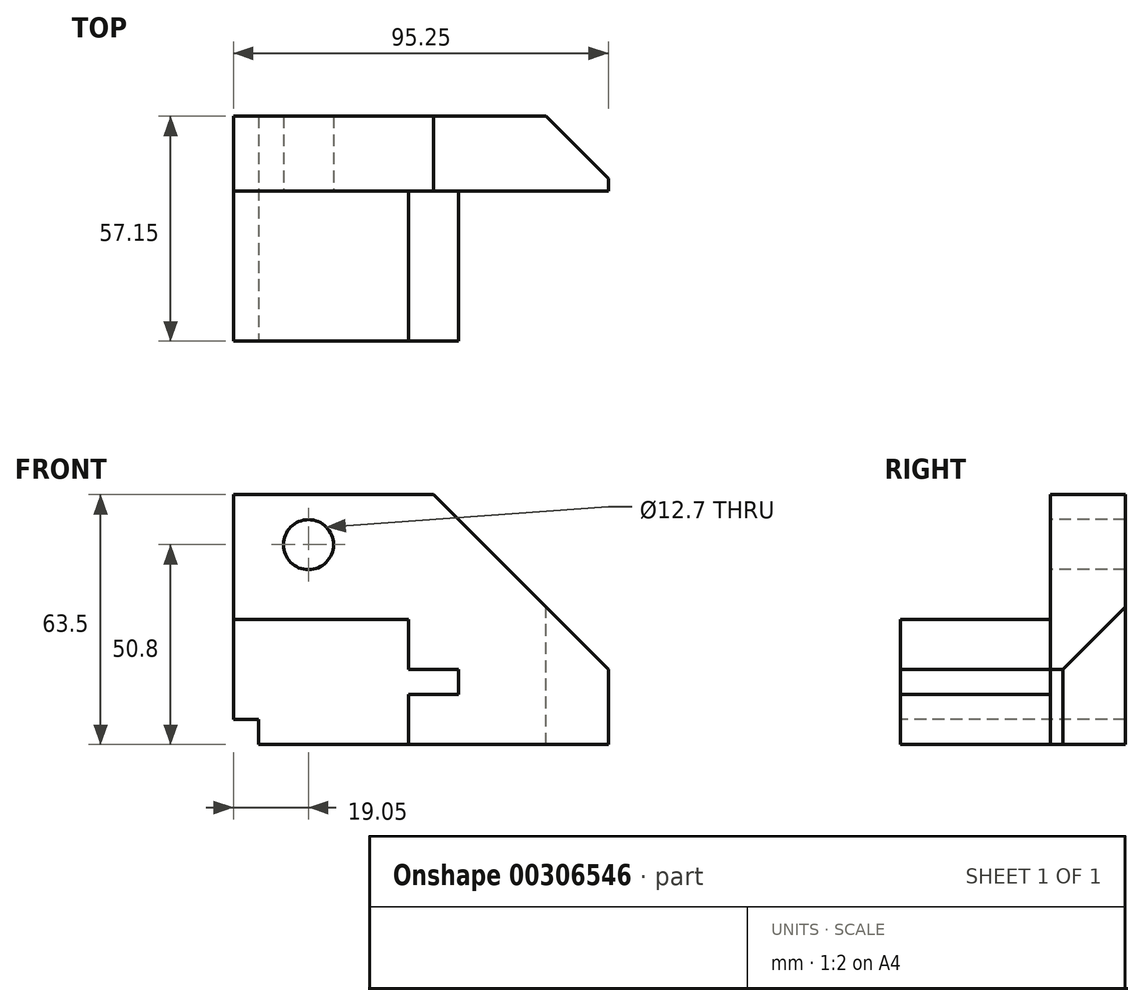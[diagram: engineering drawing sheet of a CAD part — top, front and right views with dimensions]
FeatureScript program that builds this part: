
annotation { "Feature Type Name" : "Feature", "Feature Type Description" : "" }
export const myFeature = defineFeature(function(context is Context, id is Id, definition is map)
    precondition{}
    {
        {
            var Q0;
            Q0=qCreatedBy(makeId("Front.planeOp"),FACE);
            var sketch = newSketch(context, id + "F0", { "sketchPlane" : qUnion([Q0])});
            skLineSegment(sketch, "E0.bottom", {"start": v(0, 0) * mm, "end": v(107.95, 0) * mm});
            skLineSegment(sketch, "E0.top", {"start": v(0, 63.5) * mm, "end": v(107.95, 63.5) * mm});
            skLineSegment(sketch, "E0.left", {"start": v(0, 0) * mm, "end": v(0, 63.5) * mm});
            skLineSegment(sketch, "E0.right", {"start": v(107.95, 0) * mm, "end": v(107.95, 63.5) * mm});
            skSolve(sketch);
        }
        {
            var Q0;
            Q0=makeQuery(id+"F0.imprint","IMPRINT",FACE,{"disambiguationData":[TD([[makeQuery(id+"F0.imprint","IMPRINT",EDGE,{"derivedFrom":sQuery(id+"F0.wireOp",EDGE,"E0.bottom")}),1.0]])]});
            extrude(context, id + "F1", {"entities" : qUnion([Q0]), "depth" : 57.15 * mm});
        }
        {
            var Q0;
            Q0=makeQuery(id+"F1.opExtrude","CAP_FACE",FACE,{"disambiguationData":[OSD([sQuery(id+"F0.wireOp",EDGE,"E0.bottom"),sQuery(id+"F0.wireOp",EDGE,"E0.top"),sQuery(id+"F0.wireOp",EDGE,"E0.left"),sQuery(id+"F0.wireOp",EDGE,"E0.right")])],"isStart":false});
            var sketch = newSketch(context, id + "F2", { "sketchPlane" : qUnion([Q0])});
            skLineSegment(sketch, "E1.bottom", {"start": v(0, 0) * mm, "end": v(6.35, 0) * mm});
            skLineSegment(sketch, "E1.top", {"start": v(0, 6.35) * mm, "end": v(6.35, 6.35) * mm});
            skLineSegment(sketch, "E1.left", {"start": v(0, 0) * mm, "end": v(0, 6.35) * mm});
            skLineSegment(sketch, "E1.right", {"start": v(6.35, 0) * mm, "end": v(6.35, 6.35) * mm});
            skSolve(sketch);
        }
        {
            var Q0;
            Q0 = qSketchRegion(id + "F2", true);
            extrude(context, id + "F3", {"entities" : qUnion([Q0]), "operationType" : NewBodyOperationType.REMOVE, "endBound" : BoundingType.THROUGH_ALL, "oppositeDirection" : true, "depth" : 25.4 * mm});
        }
        {
            var Q0;
            Q0=makeQuery(id+"F1.opExtrude","CAP_FACE",FACE,{"disambiguationData":[OSD([sQuery(id+"F0.wireOp",EDGE,"E0.bottom"),sQuery(id+"F0.wireOp",EDGE,"E0.top"),sQuery(id+"F0.wireOp",EDGE,"E0.left"),sQuery(id+"F0.wireOp",EDGE,"E0.right")])],"isStart":false});
            var sketch = newSketch(context, id + "F4", { "sketchPlane" : qUnion([Q0])});
            skLineSegment(sketch, "E2.bottom", {"start": v(107.95, 0) * mm, "end": v(95.25, 0) * mm});
            skLineSegment(sketch, "E2.top", {"start": v(107.95, 63.5) * mm, "end": v(95.25, 63.5) * mm});
            skLineSegment(sketch, "E2.left", {"start": v(107.95, 0) * mm, "end": v(107.95, 63.5) * mm});
            skLineSegment(sketch, "E2.right", {"start": v(95.25, 0) * mm, "end": v(95.25, 63.5) * mm});
            skSolve(sketch);
        }
        {
            var Q0;
            Q0 = qSketchRegion(id + "F4", true);
            extrude(context, id + "F5", {"entities" : qUnion([Q0]), "operationType" : NewBodyOperationType.REMOVE, "endBound" : BoundingType.THROUGH_ALL, "oppositeDirection" : true, "depth" : 25.4 * mm});
        }
        {
            var Q0;
            Q0=makeQuery(id+"F1.opExtrude","SWEPT_FACE",FACE,{"disambiguationData":[OSD([sQuery(id+"F0.wireOp",EDGE,"E0.top")])]});
            var sketch = newSketch(context, id + "F6", { "sketchPlane" : qUnion([Q0])});
            skLineSegment(sketch, "E3", {"start": v(95.25, 0) * mm, "end": v(95.25, -15.88) * mm});
            skLineSegment(sketch, "E4", {"start": v(95.25, -15.88) * mm, "end": v(79.38, 0) * mm});
            skLineSegment(sketch, "E5", {"start": v(79.38, 0) * mm, "end": v(95.25, 0) * mm});
            skSolve(sketch);
        }
        {
            var Q0;
            Q0 = qSketchRegion(id + "F6", true);
            extrude(context, id + "F7", {"entities" : qUnion([Q0]), "operationType" : NewBodyOperationType.REMOVE, "endBound" : BoundingType.THROUGH_ALL, "oppositeDirection" : true, "depth" : 25.4 * mm});
        }
        {
            var Q0;
            Q0=makeQuery(id+"F1.opExtrude","CAP_FACE",FACE,{"disambiguationData":[OSD([sQuery(id+"F0.wireOp",EDGE,"E0.bottom"),sQuery(id+"F0.wireOp",EDGE,"E0.top"),sQuery(id+"F0.wireOp",EDGE,"E0.left"),sQuery(id+"F0.wireOp",EDGE,"E0.right")])],"isStart":false});
            var sketch = newSketch(context, id + "F8", { "sketchPlane" : qUnion([Q0])});
            skLineSegment(sketch, "E6", {"start": v(0, 63.5) * mm, "end": v(0, 31.75) * mm});
            skLineSegment(sketch, "E7", {"start": v(0, 31.75) * mm, "end": v(44.45, 31.75) * mm});
            skLineSegment(sketch, "E8", {"start": v(44.45, 31.75) * mm, "end": v(44.45, 19.05) * mm});
            skLineSegment(sketch, "E9", {"start": v(44.45, 19.05) * mm, "end": v(57.15, 19.05) * mm});
            skLineSegment(sketch, "E10", {"start": v(57.15, 19.05) * mm, "end": v(57.15, 12.7) * mm});
            skLineSegment(sketch, "E11", {"start": v(57.15, 12.7) * mm, "end": v(44.45, 12.7) * mm});
            skLineSegment(sketch, "E12", {"start": v(44.45, 12.7) * mm, "end": v(44.45, 0) * mm});
            skLineSegment(sketch, "E13", {"start": v(44.45, 0) * mm, "end": v(95.25, 0) * mm});
            skLineSegment(sketch, "E14", {"start": v(95.25, 0) * mm, "end": v(95.25, 63.5) * mm});
            skLineSegment(sketch, "E15", {"start": v(95.25, 63.5) * mm, "end": v(0, 63.5) * mm});
            skSolve(sketch);
        }
        {
            var Q0;
            Q0 = qSketchRegion(id + "F8", true);
            extrude(context, id + "F9", {"entities" : qUnion([Q0]), "operationType" : NewBodyOperationType.REMOVE, "oppositeDirection" : true, "depth" : 38.1 * mm});
        }
        {
            var Q0;
            Q0=makeQuery(id+"F9.boolean.opBoolean","COPY",FACE,{"derivedFrom":makeQuery(id+"F9.opExtrude","CAP_FACE",FACE,{"disambiguationData":[OSD([sQuery(id+"F8.wireOp",EDGE,"E6"),sQuery(id+"F8.wireOp",EDGE,"E7"),sQuery(id+"F8.wireOp",EDGE,"E8"),sQuery(id+"F8.wireOp",EDGE,"E9"),sQuery(id+"F8.wireOp",EDGE,"E10"),sQuery(id+"F8.wireOp",EDGE,"E11"),sQuery(id+"F8.wireOp",EDGE,"E12"),sQuery(id+"F8.wireOp",EDGE,"E13"),sQuery(id+"F8.wireOp",EDGE,"E14"),sQuery(id+"F8.wireOp",EDGE,"E15")])],"isStart":false})});
            var sketch = newSketch(context, id + "F10", { "sketchPlane" : qUnion([Q0])});
            skLineSegment(sketch, "E16", {"start": v(95.25, 63.5) * mm, "end": v(95.25, 19.05) * mm});
            skLineSegment(sketch, "E17", {"start": v(95.25, 19.05) * mm, "end": v(50.8, 63.5) * mm});
            skLineSegment(sketch, "E18", {"start": v(50.8, 63.5) * mm, "end": v(95.25, 63.5) * mm});
            skSolve(sketch);
        }
        {
            var Q0;
            Q0 = qSketchRegion(id + "F10", true);
            extrude(context, id + "F11", {"entities" : qUnion([Q0]), "operationType" : NewBodyOperationType.REMOVE, "oppositeDirection" : true, "depth" : 25.4 * mm});
        }
        {
            var Q0;
            Q0=makeQuery(id+"F9.boolean.opBoolean","COPY",FACE,{"derivedFrom":makeQuery(id+"F9.opExtrude","CAP_FACE",FACE,{"disambiguationData":[OSD([sQuery(id+"F8.wireOp",EDGE,"E6"),sQuery(id+"F8.wireOp",EDGE,"E7"),sQuery(id+"F8.wireOp",EDGE,"E8"),sQuery(id+"F8.wireOp",EDGE,"E9"),sQuery(id+"F8.wireOp",EDGE,"E10"),sQuery(id+"F8.wireOp",EDGE,"E11"),sQuery(id+"F8.wireOp",EDGE,"E12"),sQuery(id+"F8.wireOp",EDGE,"E13"),sQuery(id+"F8.wireOp",EDGE,"E14"),sQuery(id+"F8.wireOp",EDGE,"E15")])],"isStart":false})});
            var sketch = newSketch(context, id + "F12", { "sketchPlane" : qUnion([Q0])});
            skCircle(sketch, "E19", {"center": v(19.05, 50.8) * mm, "radius": 6.35 * mm});
            skSolve(sketch);
        }
        {
            var Q0;
            Q0 = qSketchRegion(id + "F12", true);
            extrude(context, id + "F13", {"entities" : qUnion([Q0]), "operationType" : NewBodyOperationType.REMOVE, "oppositeDirection" : true, "depth" : 25.4 * mm});
        }
    });
